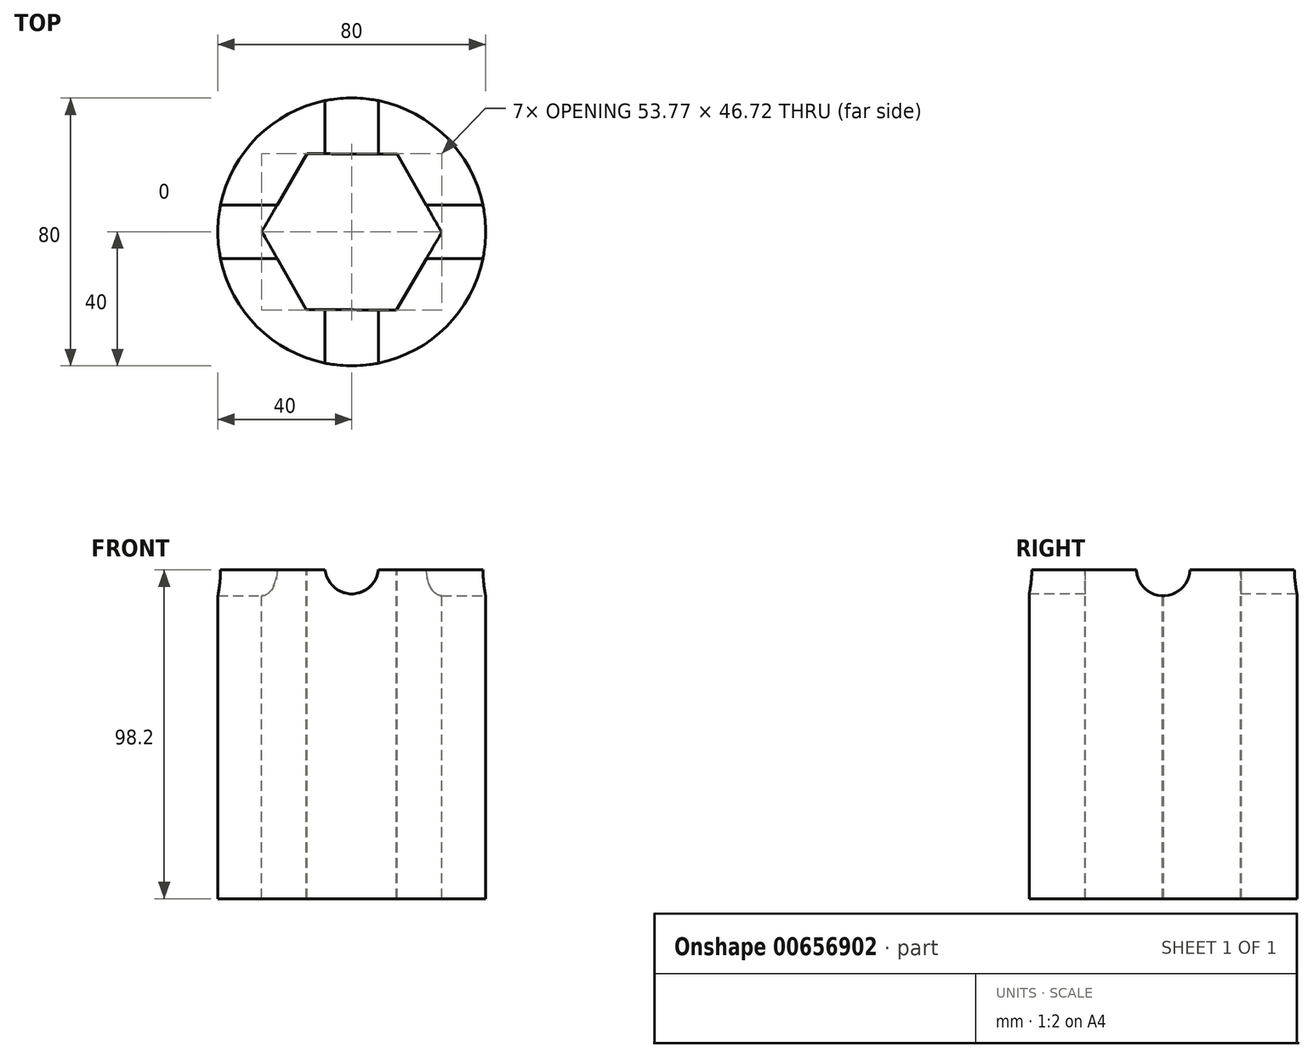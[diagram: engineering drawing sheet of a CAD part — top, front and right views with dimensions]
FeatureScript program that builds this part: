
annotation { "Feature Type Name" : "Feature", "Feature Type Description" : "" }
export const myFeature = defineFeature(function(context is Context, id is Id, definition is map)
    precondition{}
    {
        {
            var Q0;
            Q0=qCreatedBy(makeId("Top.planeOp"),FACE);
            var sketch = newSketch(context, id + "F0", { "sketchPlane" : qUnion([Q0])});
            skCircle(sketch, "E0", {"center": v(0, 0) * mm, "radius": 40 * mm});
            skSolve(sketch);
        }
        {
            var Q0;
            Q0=makeQuery(id+"F0.imprint","IMPRINT",FACE,{"disambiguationData":[TD([[makeQuery(id+"F0.imprint","IMPRINT",EDGE,{"derivedFrom":sQuery(id+"F0.wireOp",EDGE,"E0")}),1.0]])]});
            extrude(context, id + "F1", {"entities" : qUnion([Q0]), "depth" : 98.2 * mm, "offsetDistance" : 25 * mm});
        }
        {
            var Q0;
            Q0=makeQuery(id+"F1.opExtrude","CAP_FACE",FACE,{"disambiguationData":[OSD([sQuery(id+"F0.wireOp",EDGE,"E0")])],"isStart":false});
            var sketch = newSketch(context, id + "F2", { "sketchPlane" : qUnion([Q0])});
            skCircle(sketch, "E1.cCircle", {"center": v(0, 0) * mm, "radius": 23.28 * mm, "construction": true});
            skLineSegment(sketch, "E1.0", {"start": v(13.58, 23.2) * mm, "end": v(26.88, -0.16) * mm});
            skLineSegment(sketch, "E1.1", {"start": v(26.88, -0.16) * mm, "end": v(13.3, -23.36) * mm});
            skLineSegment(sketch, "E1.2", {"start": v(13.3, -23.36) * mm, "end": v(-13.58, -23.2) * mm});
            skLineSegment(sketch, "E1.3", {"start": v(-13.58, -23.2) * mm, "end": v(-26.88, 0.16) * mm});
            skLineSegment(sketch, "E1.4", {"start": v(-26.88, 0.16) * mm, "end": v(-13.3, 23.36) * mm});
            skLineSegment(sketch, "E1.5", {"start": v(-13.3, 23.36) * mm, "end": v(13.58, 23.2) * mm});
            skPoint(sketch, "E1.0.midPoint", {"position": v(20.23, 11.52) * mm});
            skSolve(sketch);
        }
        {
            var Q0;
            Q0=makeQuery(id+"F2.imprint","IMPRINT",FACE,{"disambiguationData":[TD([[makeQuery(id+"F2.imprint","IMPRINT",EDGE,{"derivedFrom":sQuery(id+"F2.wireOp",EDGE,"E1.0")}),-1.0]])]});
            extrude(context, id + "F3", {"entities" : qUnion([Q0]), "operationType" : NewBodyOperationType.REMOVE, "oppositeDirection" : true, "depth" : 100 * mm, "offsetDistance" : 25 * mm});
        }
        {
            var Q0;
            Q0=qCreatedBy(makeId("Front.planeOp"),FACE);
            cPlane(context, id + "F4", {"entities" : qUnion([Q0]), "cplaneType" : CPlaneType.OFFSET, "offset" : 45 * mm, "width" : 150 * mm, "height" : 150 * mm});
        }
        {
            var Q0;
            Q0=qCreatedBy(id+"F4.planeOp",FACE);
            var sketch = newSketch(context, id + "F5", { "sketchPlane" : qUnion([Q0])});
            skCircle(sketch, "E2", {"center": v(0, 381.98) * mm, "radius": 8 * mm});
            skCircle(sketch, "E3", {"center": v(0, 99.06) * mm, "radius": 8 * mm});
            skLineSegment(sketch, "E4", {"start": v(0, 0) * mm, "end": v(0, 99.06) * mm, "construction": true});
            skSolve(sketch);
        }
        {
            var Q0;
            Q0=makeQuery(id+"F5.imprint","IMPRINT",FACE,{"disambiguationData":[TD([[makeQuery(id+"F5.imprint","IMPRINT",EDGE,{"derivedFrom":sQuery(id+"F5.wireOp",EDGE,"E3")}),1.0]])]});
            extrude(context, id + "F6", {"entities" : qUnion([Q0]), "operationType" : NewBodyOperationType.REMOVE, "oppositeDirection" : true, "depth" : 200 * mm, "offsetDistance" : 25 * mm});
        }
        {
            var Q0;
            Q0=qCreatedBy(makeId("Right.planeOp"),FACE);
            cPlane(context, id + "F7", {"entities" : qUnion([Q0]), "cplaneType" : CPlaneType.OFFSET, "offset" : 50 * mm, "width" : 150 * mm, "height" : 150 * mm});
        }
        {
            var Q0;
            Q0=qCreatedBy(id+"F7.planeOp",FACE);
            var sketch = newSketch(context, id + "F8", { "sketchPlane" : qUnion([Q0])});
            skCircle(sketch, "E5", {"center": v(0, 98.49) * mm, "radius": 8 * mm});
            skSolve(sketch);
        }
        {
            var Q0;
            Q0=makeQuery(id+"F8.imprint","IMPRINT",FACE,{"disambiguationData":[TD([[makeQuery(id+"F8.imprint","IMPRINT",EDGE,{"derivedFrom":sQuery(id+"F8.wireOp",EDGE,"E5")}),1.0]])]});
            extrude(context, id + "F9", {"entities" : qUnion([Q0]), "operationType" : NewBodyOperationType.REMOVE, "oppositeDirection" : true, "depth" : 100 * mm, "offsetDistance" : 25 * mm});
        }
    });
